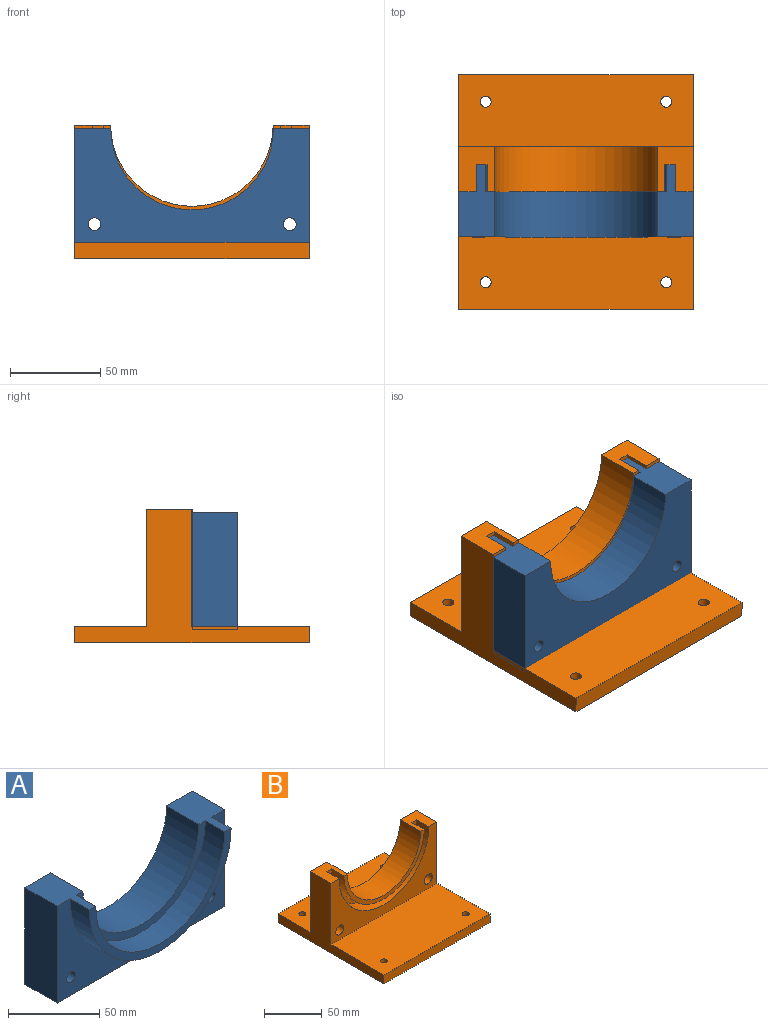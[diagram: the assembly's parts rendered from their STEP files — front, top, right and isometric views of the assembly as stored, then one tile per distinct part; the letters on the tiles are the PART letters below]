
ASSEMBLY  parts=2 mates=1
PART A: 14 faces, bbox 130x40x65 mm
  f0: plane 40x20mm, normal (0,0,1), area 575mm2, adj f5,f7,f8,f9,f10,f11,f12,f13
  f1: plane 40x20mm, normal (0,0,1), area 575mm2, adj f2,f7,f8,f9,f10,f11,f12,f13
  f2: plane 65x25mm, normal (-1,0,0), area 1625mm2, adj f1,f3,f7,f8
  f3: plane 130x25mm, normal (0,0,-1), area 3250mm2, adj f2,f5,f7,f8
  f4: cylinder r=3.55mm len=25mm, axis (0,1,0), area 557.6mm2, adj f7,f8
  f5: plane 65x25mm, normal (1,0,0), area 1625mm2, adj f0,f3,f7,f8
  f6: cylinder r=3.55mm len=25mm, axis (0,1,0), area 557.6mm2, adj f7,f8
  f7: plane 130x65mm, normal (0,-1,0), area 3619.2mm2, adj f0,f1,f2,f3,f4,f5,f6,f9
  f8: plane 130x65mm, normal (0,1,0), area 5190mm2, adj f0,f1,f2,f3,f4,f5,f6,f12
  f9: cylinder r=55mm len=110mm, axis (0,1,0), area 2591.8mm2, adj f0,f1,f7,f11
  f10: cylinder r=50mm len=100mm, axis (0,1,0), area 2356.2mm2, adj f0,f1,f11,f13
  f11: plane 110x55mm, normal (0,-1,0), area 824.7mm2, adj f0,f1,f9,f10
  f12: cylinder r=45mm len=90mm, axis (0,1,0), area 3534.3mm2, adj f0,f1,f8,f13
  f13: plane 100x50mm, normal (0,-1,0), area 746.1mm2, adj f0,f1,f10,f12
PART B: 22 faces, bbox 130x130x74.2 mm
  f0: plane 130x74.18mm, normal (1,0,0), area 2818.2mm2, adj f1,f7,f8,f9,f10,f11,f12,f13
  f1: plane 25x20mm, normal (0,0,1), area 411.5mm2, adj f0,f2,f7,f8,f14,f15,f16,f17
  f2: cylinder r=55.1mm len=110.2mm, axis (0,1,0), area 2596.5mm2, adj f1,f3,f7,f14
  f3: plane 25x20mm, normal (0,0,1), area 411.5mm2, adj f2,f5,f7,f8,f14,f15,f16,f17
  f4: cylinder r=5mm len=25mm, axis (0,1,0), area 785.4mm2, adj f7,f8
  f5: plane 130x74.18mm, normal (-1,0,0), area 2818.2mm2, adj f3,f7,f8,f9,f10,f11,f12,f13
  f6: cylinder r=5mm len=25mm, axis (0,1,0), area 785.4mm2, adj f7,f8
  f7: plane 130x65mm, normal (0,-1,0), area 3524mm2, adj f0,f1,f2,f3,f4,f5,f6,f9
  f8: plane 130x65mm, normal (0,1,0), area 5112.1mm2, adj f0,f1,f3,f4,f5,f6,f12,f16
  f9: plane 130x65mm, normal (0,0,1), area 8391.6mm2, adj f0,f5,f7,f11,f20,f21
  f10: plane 130x130mm, normal (0,0,-1), area 16783.3mm2, adj f0,f5,f11,f13,f18,f19,f20,f21
  f11: plane 130x9.18mm, normal (0,-1,0), area 1193.2mm2, adj f0,f5,f9,f10
  f12: plane 130x40mm, normal (0,0,1), area 5141.6mm2, adj f0,f5,f8,f13,f18,f19
  f13: plane 130x9.18mm, normal (0,1,0), area 1193.2mm2, adj f0,f5,f10,f12
  f14: plane 110.2x55.1mm, normal (0,-1,0), area 966.6mm2, adj f1,f2,f3,f15
  f15: cylinder r=49.2mm len=98.4mm, axis (0,1,0), area 2318.5mm2, adj f1,f3,f14,f17
  f16: cylinder r=45mm len=90mm, axis (0,1,0), area 3534.3mm2, adj f1,f3,f8,f17
  f17: plane 98.4x49.2mm, normal (0,-1,0), area 621.5mm2, adj f1,f3,f15,f16
  f18: cylinder r=3.05mm len=9.18mm, axis (0,0,-1), area 175.8mm2, adj f10,f12
  f19: cylinder r=3.05mm len=9.18mm, axis (0,0,-1), area 175.8mm2, adj f10,f12
  f20: cylinder r=3.05mm len=9.18mm, axis (0,0,-1), area 175.8mm2, adj f9,f10
  f21: cylinder r=3.05mm len=9.18mm, axis (0,0,-1), area 175.8mm2, adj f9,f10
PLACE A rot(axis=(0,0,1),180deg) t=(172.47,-145.06,72.26)mm
PLACE B t=(173.82,-95.06,103.97)mm
MATE fastened A.f4 <-> B.f6  axis (0,1,0) through (228.01,-120.06,49.04)mm
